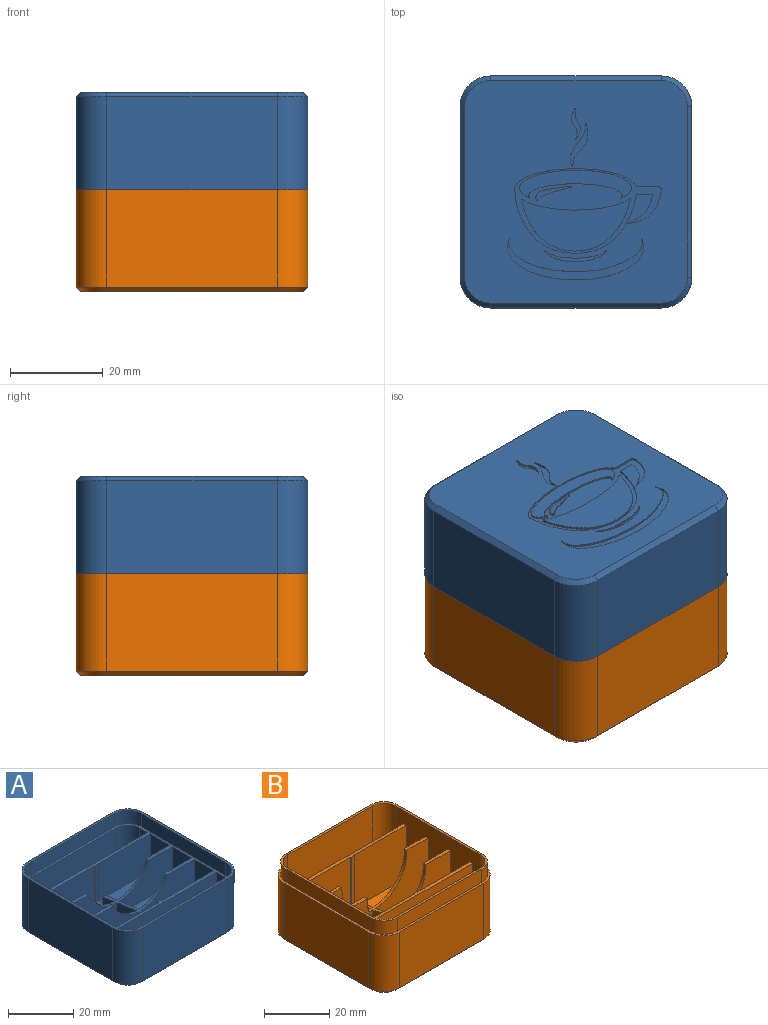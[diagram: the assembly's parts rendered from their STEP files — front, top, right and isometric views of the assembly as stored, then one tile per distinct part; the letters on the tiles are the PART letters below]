
ASSEMBLY  parts=2 mates=1
PART A: 95 faces, bbox 50.2x50.2x21.2 mm
  f0: plane 48x48mm, normal (0,0,-1), area 1807.3mm2, adj f10,f11,f12,f13,f14,f15,f16,f17
  f1: plane 50x50mm, normal (0,0,1), area 149.9mm2, adj f2,f3,f4,f5,f6,f7,f8,f9
  f2: plane 36.8x20mm, normal (0,-1,0), area 736mm2, adj f1,f6,f9,f11
  f3: plane 36.8x20mm, normal (1,0,0), area 736mm2, adj f1,f6,f7,f12
  f4: plane 36.8x20mm, normal (0,1,0), area 736mm2, adj f1,f7,f8,f16
  f5: plane 36.8x20mm, normal (-1,0,0), area 736mm2, adj f1,f8,f9,f15
  f6: cylinder r=6.6mm len=20mm, axis (0,0,1), area 207.3mm2, adj f1,f2,f3,f10
  f7: cylinder r=6.6mm len=20mm, axis (0,0,-1), area 207.3mm2, adj f1,f3,f4,f14
  f8: cylinder r=6.6mm len=20mm, axis (0,0,1), area 207.3mm2, adj f1,f4,f5,f17
  f9: cylinder r=6.6mm len=20mm, axis (0,0,-1), area 207.3mm2, adj f1,f2,f5,f13
  f10: cone r=5.6mm half-angle=45deg, axis (0,0,1), area 13.6mm2, adj f0,f6,f11,f12
  f11: plane 36.8x1mm, normal (0,-0.71,-0.71), area 52mm2, adj f0,f2,f10,f13
  f12: plane 36.8x1mm, normal (0.71,0,-0.71), area 52mm2, adj f0,f3,f10,f14
  f13: cone r=5.6mm half-angle=45deg, axis (0,0,1), area 13.6mm2, adj f0,f9,f11,f15
  f14: cone r=5.6mm half-angle=45deg, axis (0,0,1), area 13.6mm2, adj f0,f7,f12,f16
  f15: plane 36.8x1mm, normal (-0.71,0,-0.71), area 52mm2, adj f0,f5,f13,f17
  f16: plane 36.8x1mm, normal (0,0.71,-0.71), area 52mm2, adj f0,f4,f14,f17
  f17: cone r=5.6mm half-angle=45deg, axis (0,0,1), area 13.6mm2, adj f0,f8,f15,f16
  f18: plane 48.47x48.47mm, normal (0,0,1), area 311.1mm2, adj f19,f20,f21,f22,f23,f24,f25,f26
  f19: plane 36.78x5mm, normal (0,1,0), area 183.9mm2, adj f1,f18,f20,f26
  f20: cylinder r=5.8mm len=5.8mm, axis (0,0,1), area 45.6mm2, adj f1,f18,f19,f21
  f21: plane 36.78x5mm, normal (-1,0,0), area 183.9mm2, adj f1,f18,f20,f22
  f22: cylinder r=5.81mm len=5.81mm, axis (0,0,1), area 45.6mm2, adj f1,f18,f21,f23
  f23: plane 36.78x5mm, normal (0,-1,0), area 183.9mm2, adj f1,f18,f22,f24
  f24: cylinder r=5.81mm len=5.81mm, axis (0,0,1), area 45.6mm2, adj f1,f18,f23,f25
  f25: plane 36.78x5mm, normal (1,0,0), area 183.9mm2, adj f1,f18,f24,f26
  f26: cylinder r=5.8mm len=5.81mm, axis (0,0,1), area 45.6mm2, adj f1,f18,f19,f25
  f27: plane 46.78x8.4mm, normal (0,0,1), area 382mm2, adj f28,f29,f30,f31,f32,f33
  f28: cylinder r=5mm len=14mm, axis (0,0,1), area 110mm2, adj f18,f27,f29,f31
  f29: plane 14x3.4mm, normal (-1,0,0), area 47.5mm2, adj f18,f27,f28,f32
  f30: cylinder r=5mm len=14mm, axis (0,0,-1), area 110mm2, adj f18,f27,f31,f33
  f31: plane 36.78x14mm, normal (0,1,0), area 514.9mm2, adj f18,f27,f28,f30
  f32: plane 46.78x14mm, normal (0,-1,0), area 654.9mm2, adj f18,f27,f29,f33
  f33: plane 14x3.4mm, normal (1,0,0), area 47.5mm2, adj f18,f27,f30,f32
  f34: plane 3.51x1.2mm, normal (0,1,0), area 4.2mm2, adj f35,f59,f62,f64
  f35: cylinder r=18.5mm len=3mm, axis (0,1,0), area 3.6mm2, adj f34,f59,f62,f63
  f36: plane 8.4x6.12mm, normal (1,0,0), area 46.3mm2, adj f38,f45,f46,f64
  f37: plane 22.79x8.4mm, normal (0,0,1), area 191.3mm2, adj f56,f57,f58,f59
  f38: plane 22.79x8.4mm, normal (0,0,1), area 191.3mm2, adj f36,f44,f45,f46
  f39: plane 22.79x8.4mm, normal (0,0,1), area 191.3mm2, adj f47,f48,f49,f50
  f40: plane 22.79x8.4mm, normal (0,0,1), area 191.3mm2, adj f51,f52,f53,f65
  f41: plane 8.4x6.12mm, normal (-1,0,0), area 46.3mm2, adj f42,f54,f55,f64
  f42: plane 22.79x8.4mm, normal (0,0,1), area 191.3mm2, adj f41,f54,f55,f66
  f43: plane 22.79x8.4mm, normal (0,0,1), area 191.3mm2, adj f60,f61,f62,f67
  f44: plane 14x8.4mm, normal (-1,0,0), area 117.5mm2, adj f18,f38,f45,f46
  f45: plane 22.79x14mm, normal (0,-1,0), area 237.4mm2, adj f18,f36,f38,f44,f64
  f46: plane 22.79x14mm, normal (0,1,0), area 255.9mm2, adj f18,f36,f38,f44,f64
  f47: plane 14x8.4mm, normal (-1,0,0), area 117.5mm2, adj f18,f39,f48,f49
  f48: plane 22.79x14mm, normal (0,-1,0), area 258.4mm2, adj f18,f39,f47,f50,f64
  f49: plane 22.79x14mm, normal (0,1,0), area 319.1mm2, adj f18,f39,f47,f50
  f50: plane 14.24x8.64mm, normal (1,0,0), area 70.3mm2, adj f18,f39,f48,f49,f64,f68
  f51: plane 22.79x14mm, normal (0,1,0), area 319.1mm2, adj f18,f40,f53,f65
  f52: plane 22.79x14mm, normal (0,-1,0), area 258.4mm2, adj f18,f40,f53,f64,f65
  f53: plane 14.24x8.64mm, normal (-1,0,0), area 70.3mm2, adj f18,f40,f51,f52,f64,f68
  f54: plane 22.79x14mm, normal (0,1,0), area 255.9mm2, adj f18,f41,f42,f64,f66
  f55: plane 22.79x14mm, normal (0,-1,0), area 237.4mm2, adj f18,f41,f42,f64,f66
  f56: plane 14x8.4mm, normal (-1,0,0), area 117.5mm2, adj f18,f37,f57,f58
  f57: plane 22.79x14mm, normal (0,-1,0), area 319.1mm2, adj f18,f37,f56,f59
  f58: plane 22.79x14mm, normal (0,1,0), area 234.5mm2, adj f18,f37,f56,f59,f64
  f59: plane 14x8.4mm, normal (1,0,0), area 28mm2, adj f18,f34,f35,f37,f57,f58,f63,f64
  f60: plane 22.79x14mm, normal (0,1,0), area 234.5mm2, adj f18,f43,f62,f64,f67
  f61: plane 22.79x14mm, normal (0,-1,0), area 319.1mm2, adj f18,f43,f62,f67
  f62: plane 14x8.4mm, normal (-1,0,0), area 28mm2, adj f18,f34,f35,f43,f60,f61,f63,f64
  f63: plane 13.5x1.2mm, normal (0,-1,0), area 16.2mm2, adj f18,f35,f59,f62
  f64: cone r=15mm half-angle=8.1deg, axis (0,1,0), area 100.6mm2, adj f18,f34,f36,f41,f45,f46,f48,f50
  f65: plane 14x8.4mm, normal (1,0,0), area 117.5mm2, adj f18,f40,f51,f52
  f66: plane 14x8.4mm, normal (1,0,0), area 117.5mm2, adj f18,f42,f54,f55
  f67: plane 14x8.4mm, normal (1,0,0), area 117.5mm2, adj f18,f43,f60,f61
  f68: cone r=12mm half-angle=68.2deg, axis (0,1,0), area 10.2mm2, adj f18,f50,f53,f64
  f69: plane 46.78x8.4mm, normal (0,0,1), area 382mm2, adj f70,f71,f72,f73,f74,f75
  f70: cylinder r=5mm len=14mm, axis (0,0,-1), area 110mm2, adj f18,f69,f71,f73
  f71: plane 14x3.4mm, normal (-1,0,0), area 47.5mm2, adj f18,f69,f70,f74
  f72: cylinder r=5mm len=14mm, axis (0,0,1), area 110mm2, adj f18,f69,f73,f75
  f73: plane 36.78x14mm, normal (0,-1,0), area 514.9mm2, adj f18,f69,f70,f72
  f74: plane 46.78x14mm, normal (0,1,0), area 654.9mm2, adj f18,f69,f71,f75
  f75: plane 14x3.4mm, normal (1,0,0), area 47.5mm2, adj f18,f69,f72,f74
  f76: plane 3.43x0.4mm, normal (0,1,0), area 1.4mm2, adj f0,f77,f82,f83
  f77: extruded ~7.9x7.19mm, area 8.2mm2, adj f0,f76,f78,f83
  f78: plane 4.82x0.4mm, normal (0,-1,0), area 1.9mm2, adj f0,f77,f82,f83
  f79: extruded ~24.04x6.01mm, area 22.8mm2, adj f83,f88
  f80: extruded ~23.45x11.35mm, area 23.3mm2, adj f83,f89
  f81: extruded ~7.59x2.96mm, area 7mm2, adj f83,f90
  f82: extruded ~26.22x18.2mm, area 29.2mm2, adj f0,f76,f78,f83
  f83: plane 31.74x18.33mm, normal (0,0,-1), area 162.8mm2, adj f76,f77,f78,f79,f80,f81,f82
  f84: extruded ~6.82x1.92mm, area 5.9mm2, adj f0,f85
  f85: plane 6.98x2.23mm, normal (0,0,-1), area 4.9mm2, adj f84
  f86: extruded ~13.38x2.42mm, area 11.2mm2, adj f0,f87
  f87: plane 13.61x2.56mm, normal (0,0,-1), area 8.1mm2, adj f86
  f88: plane 24.31x6.17mm, normal (0,0,-1), area 70.5mm2, adj f79
  f89: plane 23.62x11.48mm, normal (0,0,-1), area 159.3mm2, adj f80
  f90: plane 7.72x3.01mm, normal (0,0,-1), area 6mm2, adj f81
  f91: extruded ~29.45x8.96mm, area 29.8mm2, adj f0,f92
  f92: plane 29.59x9.19mm, normal (0,0,-1), area 50.2mm2, adj f91
  f93: extruded ~9.33x3.78mm, area 8.3mm2, adj f0,f94
  f94: plane 9.57x4.16mm, normal (0,0,-1), area 9.5mm2, adj f93
PART B: 79 faces, bbox 50.3x50.3x27.3 mm
  f0: plane 36.8x21mm, normal (0,-1,0), area 772.8mm2, adj f5,f8,f10,f17
  f1: plane 36.8x21mm, normal (1,0,0), area 772.8mm2, adj f5,f6,f11,f17
  f2: plane 36.8x21mm, normal (0,1,0), area 772.8mm2, adj f6,f7,f15,f17
  f3: plane 36.8x21mm, normal (-1,0,0), area 772.8mm2, adj f7,f8,f14,f17
  f4: plane 48x48mm, normal (0,0,-1), area 2277.1mm2, adj f9,f10,f11,f12,f13,f14,f15,f16
  f5: cylinder r=6.6mm len=21mm, axis (0,0,1), area 217.7mm2, adj f0,f1,f9,f17
  f6: cylinder r=6.6mm len=21mm, axis (0,0,-1), area 217.7mm2, adj f1,f2,f13,f17
  f7: cylinder r=6.6mm len=21mm, axis (0,0,1), area 217.7mm2, adj f2,f3,f16,f17
  f8: cylinder r=6.6mm len=21mm, axis (0,0,-1), area 217.7mm2, adj f0,f3,f12,f17
  f9: cone r=5.6mm half-angle=45deg, axis (0,0,1), area 13.6mm2, adj f4,f5,f10,f11
  f10: plane 36.8x1mm, normal (0,-0.71,-0.71), area 52mm2, adj f0,f4,f9,f12
  f11: plane 36.8x1mm, normal (0.71,0,-0.71), area 52mm2, adj f1,f4,f9,f13
  f12: cone r=5.6mm half-angle=45deg, axis (0,0,1), area 13.6mm2, adj f4,f8,f10,f14
  f13: cone r=5.6mm half-angle=45deg, axis (0,0,1), area 13.6mm2, adj f4,f6,f11,f15
  f14: plane 36.8x1mm, normal (-0.71,0,-0.71), area 52mm2, adj f3,f4,f12,f16
  f15: plane 36.8x1mm, normal (0,0.71,-0.71), area 52mm2, adj f2,f4,f13,f16
  f16: cone r=5.6mm half-angle=45deg, axis (0,0,1), area 13.6mm2, adj f4,f7,f14,f15
  f17: plane 50x50mm, normal (0,0,1), area 150.9mm2, adj f0,f1,f2,f3,f5,f6,f7,f8
  f18: plane 36.78x5mm, normal (0,-1,0), area 183.9mm2, adj f17,f19,f25,f26
  f19: cylinder r=5.8mm len=5.8mm, axis (0,0,-1), area 45.6mm2, adj f17,f18,f20,f26
  f20: plane 36.78x5mm, normal (1,0,0), area 183.9mm2, adj f17,f19,f21,f26
  f21: cylinder r=5.8mm len=5.8mm, axis (0,0,-1), area 45.6mm2, adj f17,f20,f22,f26
  f22: plane 36.78x5mm, normal (0,1,0), area 183.9mm2, adj f17,f21,f23,f26
  f23: cylinder r=5.8mm len=5.8mm, axis (0,0,-1), area 45.6mm2, adj f17,f22,f24,f26
  f24: plane 36.78x5mm, normal (-1,0,0), area 183.9mm2, adj f17,f23,f25,f26
  f25: cylinder r=5.8mm len=5.8mm, axis (0,0,-1), area 45.6mm2, adj f17,f18,f24,f26
  f26: plane 48.38x48.38mm, normal (0,0,1), area 144.8mm2, adj f18,f19,f20,f21,f22,f23,f24,f25
  f27: plane 8.4x6.12mm, normal (1,0,0), area 46.3mm2, adj f32,f36,f38,f40
  f28: cone r=12mm half-angle=68.2deg, axis (0,1,0), area 11.4mm2, adj f32,f45,f46,f47
  f29: plane 8.4x6.12mm, normal (-1,0,0), area 46.3mm2, adj f32,f60,f62,f64
  f30: cylinder r=18.5mm len=3mm, axis (0,1,0), area 3.6mm2, adj f31,f68,f69,f70
  f31: plane 3.51x1.2mm, normal (0,1,0), area 4.2mm2, adj f30,f32,f68,f70
  f32: cone r=15mm half-angle=8.1deg, axis (0,1,0), area 125.4mm2, adj f27,f28,f29,f31,f34,f35,f38,f39
  f33: plane 22.79x8.4mm, normal (0,0,1), area 191.3mm2, adj f35,f47,f48,f49
  f34: plane 1.2x1mm, normal (-0.99,0.14,0), area 1.2mm2, adj f32,f35,f37,f38
  f35: plane 22.79x20mm, normal (0,-1,0), area 324.1mm2, adj f32,f33,f34,f37,f47,f49
  f36: plane 22.79x8.4mm, normal (0,0,1), area 191.3mm2, adj f27,f38,f40,f49
  f37: plane 10.66x1.2mm, normal (0,0,1), area 12.7mm2, adj f34,f35,f38,f49
  f38: plane 22.79x20mm, normal (0,1,0), area 320.5mm2, adj f27,f32,f34,f36,f37,f49
  f39: plane 1.2x1mm, normal (-0.99,0.14,0), area 1.2mm2, adj f32,f40,f42,f43
  f40: plane 22.79x20mm, normal (0,-1,0), area 294.6mm2, adj f27,f32,f36,f39,f42,f49
  f41: plane 22.79x8.4mm, normal (0,0,1), area 191.3mm2, adj f43,f49,f68,f72
  f42: plane 9.29x1.2mm, normal (0,0,1), area 11mm2, adj f39,f40,f43,f49
  f43: plane 22.79x20mm, normal (0,1,0), area 290.7mm2, adj f32,f39,f41,f42,f49,f68
  f44: plane 46.78x8.4mm, normal (0,0,1), area 382mm2, adj f49,f50,f51,f52,f53,f54
  f45: plane 20.31x8.71mm, normal (-1,0,0), area 72.1mm2, adj f28,f32,f46,f55,f56,f57,f59
  f46: plane 5.5x1.2mm, normal (0,1,0), area 6.6mm2, adj f28,f45,f47,f56
  f47: plane 20.31x8.71mm, normal (1,0,0), area 72.1mm2, adj f28,f32,f33,f35,f46,f48,f56
  f48: plane 22.79x20mm, normal (0,1,0), area 455.8mm2, adj f33,f47,f49,f56
  f49: plane 36.78x25mm, normal (-1,0,0), area 823.5mm2, adj f26,f33,f35,f36,f37,f38,f40,f41
  f50: plane 36.78x25mm, normal (1,0,0), area 823.5mm2, adj f26,f44,f51,f54,f55,f56,f57,f59
  f51: cylinder r=5mm len=25mm, axis (0,0,-1), area 196.3mm2, adj f26,f44,f50,f52
  f52: plane 36.78x25mm, normal (0,1,0), area 919.5mm2, adj f26,f44,f51,f53
  f53: cylinder r=5mm len=25mm, axis (0,0,1), area 196.3mm2, adj f26,f44,f49,f52
  f54: plane 46.78x20mm, normal (0,-1,0), area 935.6mm2, adj f44,f49,f50,f56
  f55: plane 22.79x8.4mm, normal (0,0,1), area 191.3mm2, adj f45,f50,f57,f59
  f56: plane 46.78x1.49mm, normal (0,0,1), area 56.5mm2, adj f45,f46,f47,f48,f49,f50,f54,f57
  f57: plane 22.79x20mm, normal (0,1,0), area 455.8mm2, adj f45,f50,f55,f56
  f58: plane 1.2x1mm, normal (0.99,0.14,0), area 1.2mm2, adj f32,f59,f61,f62
  f59: plane 22.79x20mm, normal (0,-1,0), area 324.1mm2, adj f32,f45,f50,f55,f58,f61
  f60: plane 22.79x8.4mm, normal (0,0,1), area 191.3mm2, adj f29,f50,f62,f64
  f61: plane 10.66x1.2mm, normal (0,0,1), area 12.7mm2, adj f50,f58,f59,f62
  f62: plane 22.79x20mm, normal (0,1,0), area 320.5mm2, adj f29,f32,f50,f58,f60,f61
  f63: plane 1.2x1mm, normal (0.99,0.14,0), area 1.2mm2, adj f32,f64,f66,f67
  f64: plane 22.79x20mm, normal (0,-1,0), area 294.6mm2, adj f29,f32,f50,f60,f63,f66
  f65: plane 22.79x8.4mm, normal (0,0,1), area 191.3mm2, adj f50,f67,f70,f71
  f66: plane 9.29x1.2mm, normal (0,0,1), area 11mm2, adj f50,f63,f64,f67
  f67: plane 22.79x20mm, normal (0,1,0), area 290.7mm2, adj f32,f50,f63,f65,f66,f70
  f68: plane 20x8.4mm, normal (1,0,0), area 29.7mm2, adj f30,f31,f32,f41,f43,f69,f72,f73
  f69: plane 19.5x1.2mm, normal (0,-1,0), area 23.4mm2, adj f30,f68,f70,f73
  f70: plane 20x8.4mm, normal (-1,0,0), area 29.7mm2, adj f30,f31,f32,f65,f67,f69,f71,f73
  f71: plane 22.79x20mm, normal (0,-1,0), area 455.8mm2, adj f50,f65,f70,f73
  f72: plane 22.79x20mm, normal (0,-1,0), area 455.8mm2, adj f41,f49,f68,f73
  f73: plane 46.78x1.49mm, normal (0,0,1), area 56.5mm2, adj f49,f50,f68,f69,f70,f71,f72,f74
  f74: plane 46.78x20mm, normal (0,1,0), area 935.6mm2, adj f49,f50,f73,f75
  f75: plane 46.78x8.4mm, normal (0,0,1), area 382mm2, adj f49,f50,f74,f76,f77,f78
  f76: cylinder r=5mm len=25mm, axis (0,0,1), area 196.3mm2, adj f26,f50,f75,f78
  f77: cylinder r=5mm len=25mm, axis (0,0,-1), area 196.3mm2, adj f26,f49,f75,f78
  f78: plane 36.78x25mm, normal (0,-1,0), area 919.5mm2, adj f26,f75,f76,f77
PLACE A rot(axis=(0,1,0),180deg) t=(55,0,43)mm
PLACE B at identity
MATE fastened A.f9 <-> B.f5  axis (0,0,-1) through (18.4,-18.4,22)mm
